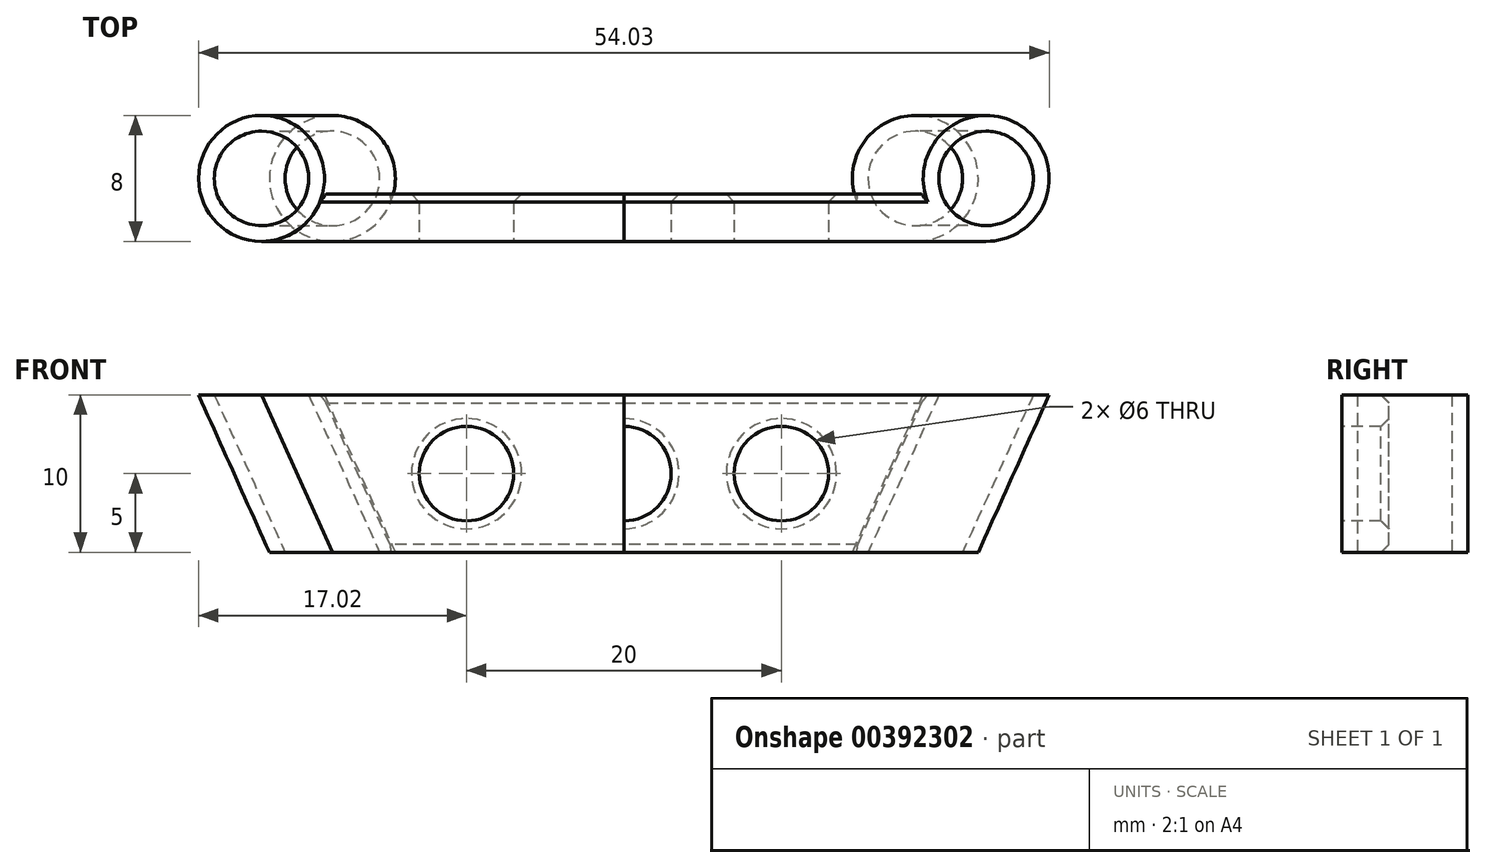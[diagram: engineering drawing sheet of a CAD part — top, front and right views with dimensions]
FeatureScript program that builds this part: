
annotation { "Feature Type Name" : "Feature", "Feature Type Description" : "" }
export const myFeature = defineFeature(function(context is Context, id is Id, definition is map)
    precondition{}
    {
        {
            var Q0;
            Q0=qCreatedBy(makeId("Front.planeOp"),FACE);
            var sketch = newSketch(context, id + "F0", { "sketchPlane" : qUnion([Q0])});
            skLineSegment(sketch, "E0", {"start": v(0, 0) * mm, "end": v(-18.5, 0) * mm});
            skLineSegment(sketch, "E1", {"start": v(-18.5, 0) * mm, "end": v(18.5, 0) * mm});
            skLineSegment(sketch, "E2", {"start": v(0, 0) * mm, "end": v(0, 10) * mm});
            skLineSegment(sketch, "E3", {"start": v(0, 10) * mm, "end": v(-23, 10) * mm});
            skLineSegment(sketch, "E4", {"start": v(-23, 10) * mm, "end": v(23, 10) * mm});
            skLineSegment(sketch, "E5", {"start": v(23, 10) * mm, "end": v(18.5, 0) * mm});
            skLineSegment(sketch, "E6", {"start": v(-23, 10) * mm, "end": v(-18.5, 0) * mm});
            skLineSegment(sketch, "E7.0", {"start": v(-19.13, 7.5) * mm, "end": v(19.13, 7.5) * mm});
            skLineSegment(sketch, "E7.1", {"start": v(-19.13, 7.5) * mm, "end": v(-16.88, 2.5) * mm});
            skLineSegment(sketch, "E7.2", {"start": v(-16.88, 2.5) * mm, "end": v(16.88, 2.5) * mm});
            skLineSegment(sketch, "E7.3", {"start": v(19.13, 7.5) * mm, "end": v(16.88, 2.5) * mm});
            skSolve(sketch);
        }
        {
            var Q0;
            Q0=qCreatedBy(makeId("Top.planeOp"),FACE);
            var sketch = newSketch(context, id + "F1", { "sketchPlane" : qUnion([Q0])});
            skCircle(sketch, "E8", {"center": v(-18.52, 0) * mm, "radius": 3 * mm});
            skCircle(sketch, "E9", {"center": v(-18.52, 0) * mm, "radius": 4 * mm});
            skCircle(sketch, "E10", {"center": v(18.5, 0) * mm, "radius": 3 * mm});
            skCircle(sketch, "E11", {"center": v(18.5, 0) * mm, "radius": 4 * mm});
            skSolve(sketch);
        }
        {
            var Q0;
            Q0=makeQuery(id+"F1.imprint","IMPRINT",FACE,{"disambiguationData":[TD([[makeQuery(id+"F1.imprint","IMPRINT",EDGE,{"derivedFrom":sQuery(id+"F1.wireOp",EDGE,"E10")}),-1.0]])]});
            var Q1;
            Q1=sQuery(id+"F0.wireOp",EDGE,"E5");
            sweep(context, id + "F2", {"profiles" : qUnion([Q0]), "path" : qUnion([Q1])});
        }
        {
            var Q0;
            Q0=makeQuery(id+"F1.imprint","IMPRINT",FACE,{"disambiguationData":[TD([[makeQuery(id+"F1.imprint","IMPRINT",EDGE,{"derivedFrom":sQuery(id+"F1.wireOp",EDGE,"E8")}),-1.0]])]});
            var Q1;
            Q1=sQuery(id+"F0.wireOp",EDGE,"E6");
            sweep(context, id + "F3", {"profiles" : qUnion([Q0]), "path" : qUnion([Q1])});
        }
        {
            var Q0;
            Q0=qCreatedBy(makeId("Right.planeOp"),FACE);
            var sketch = newSketch(context, id + "F4", { "sketchPlane" : qUnion([Q0])});
            skLineSegment(sketch, "E12", {"start": v(0, 0) * mm, "end": v(-1, 0) * mm});
            skLineSegment(sketch, "E13.bottom", {"start": v(-1, 0) * mm, "end": v(-4, 0) * mm});
            skLineSegment(sketch, "E13.top", {"start": v(-1, 10) * mm, "end": v(-4, 10) * mm});
            skLineSegment(sketch, "E13.left", {"start": v(-1, 0) * mm, "end": v(-1, 10) * mm});
            skLineSegment(sketch, "E13.right", {"start": v(-4, 0) * mm, "end": v(-4, 10) * mm});
            skSolve(sketch);
        }
        {
            var Q0;
            Q0=makeQuery(id+"F4.imprint","IMPRINT",FACE,{"disambiguationData":[TD([[makeQuery(id+"F4.imprint","IMPRINT",EDGE,{"derivedFrom":sQuery(id+"F4.wireOp",EDGE,"E13.bottom")}),-1.0]])]});
            extrude(context, id + "F5", {"entities" : qUnion([Q0]), "operationType" : NewBodyOperationType.ADD, "endBound" : BoundingType.UP_TO_NEXT, "depth" : 25 * mm});
        }
        {
            var Q0;
            Q0=makeQuery(id+"F5.opExtrude","CAP_FACE",FACE,{"disambiguationData":[OSD([sQuery(id+"F4.wireOp",EDGE,"E13.bottom"),sQuery(id+"F4.wireOp",EDGE,"E13.top"),sQuery(id+"F4.wireOp",EDGE,"E13.left"),sQuery(id+"F4.wireOp",EDGE,"E13.right")])],"isStart":true});
            extrude(context, id + "F6", {"entities" : qUnion([Q0]), "endBound" : BoundingType.UP_TO_NEXT, "depth" : 25 * mm});
        }
        {
            var Q0;
            Q0=makeQuery(id+"F5.opExtrude","SWEPT_FACE",FACE,{"disambiguationData":[OSD([sQuery(id+"F4.wireOp",EDGE,"E13.right")])]});
            var sketch = newSketch(context, id + "F7", { "sketchPlane" : qUnion([Q0])});
            skLineSegment(sketch, "E14", {"start": v(0, 5) * mm, "end": v(-10, 5) * mm});
            skLineSegment(sketch, "E15", {"start": v(-10, 5) * mm, "end": v(10, 5) * mm});
            skCircle(sketch, "E16", {"center": v(-10, 5) * mm, "radius": 3 * mm});
            skCircle(sketch, "E17", {"center": v(10, 5) * mm, "radius": 3 * mm});
            skCircle(sketch, "E18", {"center": v(0, 5) * mm, "radius": 3 * mm});
            skSolve(sketch);
        }
        {
            var Q0;
            Q0=makeQuery(id+"F7.imprint","IMPRINT",FACE,{"disambiguationData":[TD([[makeQuery(id+"F7.imprint","IMPRINT",EDGE,{"derivedFrom":sQuery(id+"F7.wireOp",EDGE,"E16")}),1.0]])]});
            var Q1;
            Q1=makeQuery(id+"F7.imprint","IMPRINT",FACE,{"disambiguationData":[TD([[makeQuery(id+"F7.imprint","IMPRINT",EDGE,{"derivedFrom":sQuery(id+"F7.wireOp",EDGE,"E17")}),1.0]])]});
            var Q2;
            {var subQ0=sQuery(id+"F7.wireOp",EDGE,"E15");var subQ1=makeQuery(id+"F5.opExtrude","CAP_EDGE",EDGE,{"disambiguationData":[OSD([sQuery(id+"F4.wireOp",EDGE,"E13.right")])],"isStart":true});var subQ2=makeQuery(id+"F7.imprint","INTERSECT",VERTEX,{"derivedFrom":[subQ1,subQ0]});Q2=makeQuery(id+"F7.imprint","IMPRINT",FACE,{"disambiguationData":[TD([[makeQuery(id+"F7.imprint","IMPRINT",EDGE,{"disambiguationData":[TD([[subQ2,1.0]])],"derivedFrom":subQ0}),1.0]])]});}
            var Q3;
            {var subQ0=sQuery(id+"F7.wireOp",EDGE,"E15");var subQ1=makeQuery(id+"F5.opExtrude","CAP_EDGE",EDGE,{"disambiguationData":[OSD([sQuery(id+"F4.wireOp",EDGE,"E13.right")])],"isStart":true});var subQ2=makeQuery(id+"F7.imprint","INTERSECT",VERTEX,{"derivedFrom":[subQ1,subQ0]});Q3=makeQuery(id+"F7.imprint","IMPRINT",FACE,{"disambiguationData":[TD([[makeQuery(id+"F7.imprint","IMPRINT",EDGE,{"disambiguationData":[TD([[subQ2,-1.0]])],"derivedFrom":subQ0}),1.0]])]});}
            var Q4;
            {var subQ0=sQuery(id+"F7.wireOp",EDGE,"E15");var subQ1=makeQuery(id+"F5.opExtrude","CAP_EDGE",EDGE,{"disambiguationData":[OSD([sQuery(id+"F4.wireOp",EDGE,"E13.right")])],"isStart":true});var subQ2=makeQuery(id+"F7.imprint","INTERSECT",VERTEX,{"derivedFrom":[subQ1,subQ0]});Q4=makeQuery(id+"F7.imprint","IMPRINT",FACE,{"disambiguationData":[TD([[makeQuery(id+"F7.imprint","IMPRINT",EDGE,{"disambiguationData":[TD([[subQ2,-1.0]])],"derivedFrom":subQ0}),-1.0]])]});}
            var Q5;
            {var subQ0=sQuery(id+"F7.wireOp",EDGE,"E15");var subQ1=makeQuery(id+"F5.opExtrude","CAP_EDGE",EDGE,{"disambiguationData":[OSD([sQuery(id+"F4.wireOp",EDGE,"E13.right")])],"isStart":true});var subQ2=makeQuery(id+"F7.imprint","INTERSECT",VERTEX,{"derivedFrom":[subQ1,subQ0]});Q5=makeQuery(id+"F7.imprint","IMPRINT",FACE,{"disambiguationData":[TD([[makeQuery(id+"F7.imprint","IMPRINT",EDGE,{"disambiguationData":[TD([[subQ2,1.0]])],"derivedFrom":subQ0}),-1.0]])]});}
            extrude(context, id + "F8", {"entities" : qUnion([Q0, Q1, Q2, Q3, Q4, Q5]), "operationType" : NewBodyOperationType.REMOVE, "oppositeDirection" : true, "depth" : 4 * mm});
        }
        {
            var Q0;
            Q0=makeQuery(id+"F8.boolean.opBoolean","INTERSECT",EDGE,{"derivedFrom":[makeQuery(id+"F5.opExtrude","SWEPT_FACE",FACE,{"disambiguationData":[OSD([sQuery(id+"F4.wireOp",EDGE,"E13.left")])]}),makeQuery(id+"F8.opExtrude","SWEPT_FACE",FACE,{"disambiguationData":[OSD([sQuery(id+"F7.wireOp",EDGE,"E17")])]})]});
            var Q1;
            Q1=makeQuery(id+"F8.boolean.opBoolean","INTERSECT",EDGE,{"derivedFrom":[makeQuery(id+"F5.opExtrude","SWEPT_FACE",FACE,{"disambiguationData":[OSD([sQuery(id+"F4.wireOp",EDGE,"E13.left")])]}),makeQuery(id+"F8.opExtrude","SWEPT_FACE",FACE,{"disambiguationData":[OSD([sQuery(id+"F7.wireOp",EDGE,"E18")])]})]});
            var Q2;
            Q2=makeQuery(id+"F8.boolean.opBoolean","INTERSECT",EDGE,{"derivedFrom":[makeQuery(id+"F6.opExtrude","SWEPT_FACE",FACE,{"disambiguationData":[OSD([sQuery(id+"F4.wireOp",EDGE,"E13.left")])]}),makeQuery(id+"F8.opExtrude","SWEPT_FACE",FACE,{"disambiguationData":[OSD([sQuery(id+"F7.wireOp",EDGE,"E18")])]})]});
            var Q3;
            Q3=makeQuery(id+"F8.boolean.opBoolean","INTERSECT",EDGE,{"derivedFrom":[makeQuery(id+"F6.opExtrude","SWEPT_FACE",FACE,{"disambiguationData":[OSD([sQuery(id+"F4.wireOp",EDGE,"E13.left")])]}),makeQuery(id+"F8.opExtrude","SWEPT_FACE",FACE,{"disambiguationData":[OSD([sQuery(id+"F7.wireOp",EDGE,"E16")])]})]});
            chamfer(context, id + "F9", {"entities" : qUnion([Q0, Q1, Q2, Q3]), "width" : 0.5 * mm, "tangentPropagation" : true});
        }
        {
            var Q0;
            Q0=makeQuery(id+"F5.opExtrude","SWEPT_EDGE",EDGE,{"disambiguationData":[OSD([sQuery(id+"F4.wireOp",EDGE,"E13.top"),sQuery(id+"F4.wireOp",EDGE,"E13.left")])]});
            var Q1;
            Q1=makeQuery(id+"F6.opExtrude","SWEPT_EDGE",EDGE,{"disambiguationData":[OSD([sQuery(id+"F4.wireOp",EDGE,"E13.top"),sQuery(id+"F4.wireOp",EDGE,"E13.left")])]});
            var Q2;
            Q2=makeQuery(id+"F6.opExtrude","SWEPT_EDGE",EDGE,{"disambiguationData":[OSD([sQuery(id+"F4.wireOp",EDGE,"E13.bottom"),sQuery(id+"F4.wireOp",EDGE,"E13.left")])]});
            var Q3;
            Q3=makeQuery(id+"F5.opExtrude","SWEPT_EDGE",EDGE,{"disambiguationData":[OSD([sQuery(id+"F4.wireOp",EDGE,"E13.bottom"),sQuery(id+"F4.wireOp",EDGE,"E13.left")])]});
            chamfer(context, id + "F10", {"entities" : qUnion([Q0, Q1, Q2, Q3]), "width" : 0.5 * mm, "tangentPropagation" : true});
        }
    });
